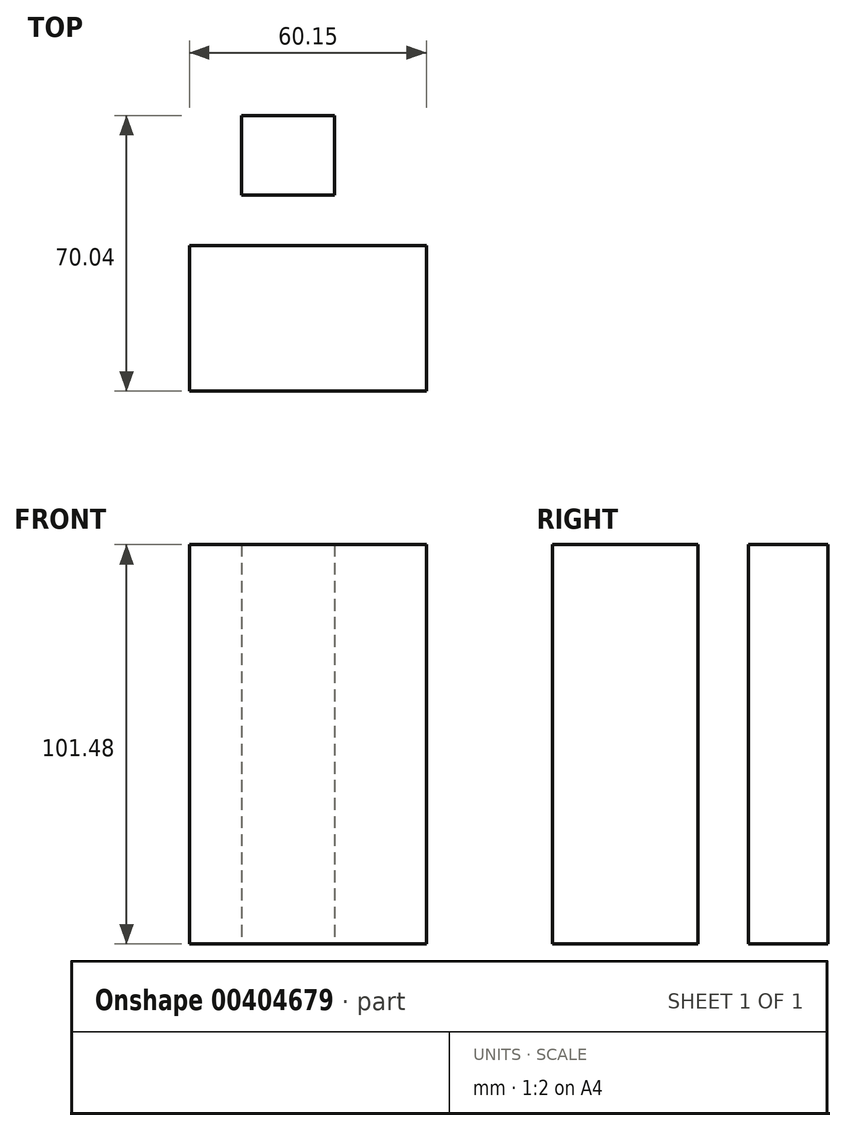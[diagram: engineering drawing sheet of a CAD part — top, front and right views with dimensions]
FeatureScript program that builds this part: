
annotation { "Feature Type Name" : "Feature", "Feature Type Description" : "" }
export const myFeature = defineFeature(function(context is Context, id is Id, definition is map)
    precondition{}
    {
        {
            var Q0;
            Q0=qCreatedBy(makeId("Top.planeOp"),FACE);
            var sketch = newSketch(context, id + "F0", { "sketchPlane" : qUnion([Q0])});
            skLineSegment(sketch, "E0.bottom", {"start": v(-36.9, -12.75) * mm, "end": v(23.25, -12.75) * mm});
            skLineSegment(sketch, "E0.top", {"start": v(-36.9, -49.8) * mm, "end": v(23.25, -49.8) * mm});
            skLineSegment(sketch, "E0.left", {"start": v(-36.9, -12.75) * mm, "end": v(-36.9, -49.8) * mm});
            skLineSegment(sketch, "E0.right", {"start": v(23.25, -12.75) * mm, "end": v(23.25, -49.8) * mm});
            skLineSegment(sketch, "E1.bottom", {"start": v(10.8, 10.05) * mm, "end": v(48.3, 10.05) * mm});
            skLineSegment(sketch, "E1.top", {"start": v(10.8, 44.1) * mm, "end": v(48.3, 44.1) * mm});
            skLineSegment(sketch, "E1.left", {"start": v(10.8, 10.05) * mm, "end": v(10.8, 44.1) * mm});
            skLineSegment(sketch, "E1.right", {"start": v(48.3, 10.05) * mm, "end": v(48.3, 44.1) * mm});
            skLineSegment(sketch, "E2.bottom", {"start": v(34.5, -8.7) * mm, "end": v(63.6, -8.7) * mm});
            skLineSegment(sketch, "E2.top", {"start": v(34.5, -34.95) * mm, "end": v(63.6, -34.95) * mm});
            skLineSegment(sketch, "E2.left", {"start": v(34.5, -8.7) * mm, "end": v(34.5, -34.95) * mm});
            skLineSegment(sketch, "E2.right", {"start": v(63.6, -8.7) * mm, "end": v(63.6, -34.95) * mm});
            skLineSegment(sketch, "E3.bottom", {"start": v(-23.7, 20.25) * mm, "end": v(0, 20.25) * mm});
            skLineSegment(sketch, "E3.top", {"start": v(-23.7, 0) * mm, "end": v(0, 0) * mm});
            skLineSegment(sketch, "E3.left", {"start": v(-23.7, 20.25) * mm, "end": v(-23.7, 0) * mm});
            skLineSegment(sketch, "E3.right", {"start": v(0, 20.25) * mm, "end": v(0, 0) * mm});
            skSolve(sketch);
        }
        {
            var Q0;
            Q0=makeQuery(id+"F0.imprint","IMPRINT",FACE,{"disambiguationData":[TD([[makeQuery(id+"F0.imprint","IMPRINT",EDGE,{"derivedFrom":sQuery(id+"F0.wireOp",EDGE,"E0.bottom")}),-1.0]])]});
            var Q1;
            Q1=makeQuery(id+"F0.imprint","IMPRINT",FACE,{"disambiguationData":[TD([[makeQuery(id+"F0.imprint","IMPRINT",EDGE,{"derivedFrom":sQuery(id+"F0.wireOp",EDGE,"E3.bottom")}),-1.0]])]});
            extrude(context, id + "F1", {"entities" : qUnion([Q0, Q1]), "depth" : 101.48 * mm});
        }
    });
